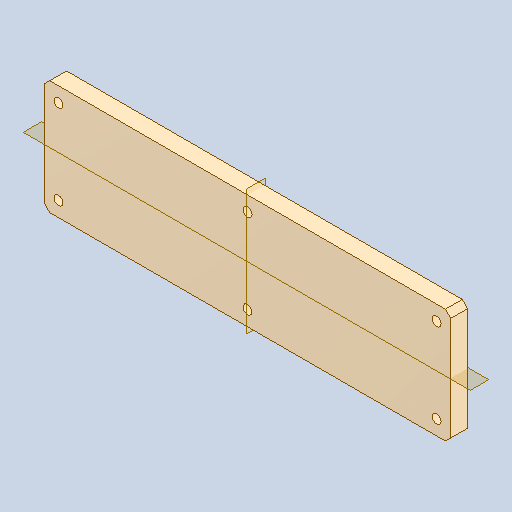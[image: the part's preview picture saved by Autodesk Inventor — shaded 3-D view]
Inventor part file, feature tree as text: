
AUTODESK INVENTOR PART (.ipt)
format: ipt  version: 2022 (Build 260153000, 153)  size: 115,200 bytes
history: native  units: mm
features: other x4, plane x2, reference x2, extrude x1, chamfer x1, hole x1, sketch x1
ambient origin geometry x8: Origin, YZ Plane, XZ Plane, XY Plane, X Axis, Y Axis, Z Axis, Center Point
bodies: Solid1 (feature_tree)
feature tree (12):
  extrude  "Extrusion1"  Depth=153.0mm
  chamfer  "Chamfer1"  Distance=6.35mm
  plane  "Work Plane1"
  plane  "Work Plane2"
  hole  "Hole1"  [1 undecoded]
  sketch  "Sketch1"  dims[d0=43.0mm d1=153.0mm d2=6.35mm d3=0.0mm d4=2.0mm d5=2.0mm d6=45.0deg d7=3.4mm d8=6.0mm d9=6.3mm d10=2.0mm d11=90.0deg d12=8.0mm d13=20.594885mm]
  reference  "Reference1"
  reference  "Reference2"
  parser-record x1  (decoder bookkeeping rows leaked as tree rows — omitted from the tree; the rows remain in map.json)
  other  "Main Body.iam"
  other  "Base Plate:2"
  other  "Base Plate:1"
note: 1 required parameter value undecoded (feature->parameter linkage not recoverable at this tier; creation-order binding heuristic only, values carry confidence <= 0.55)
note: 1 file-system path scrubbed to <path> (originals preserved in map.json)
